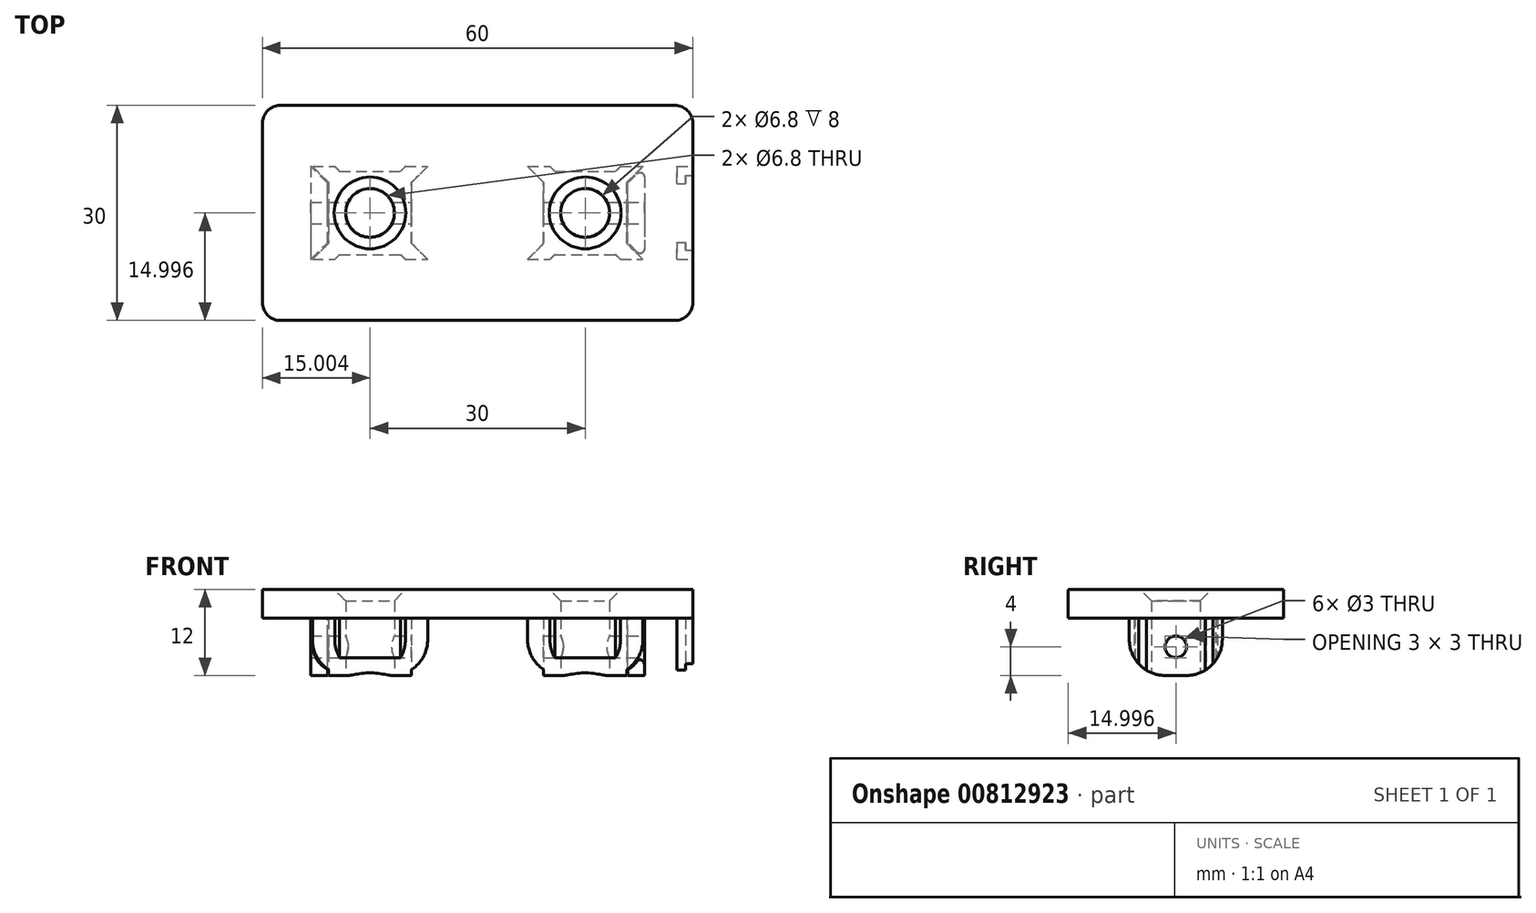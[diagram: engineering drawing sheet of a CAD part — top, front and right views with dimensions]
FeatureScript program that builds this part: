
annotation { "Feature Type Name" : "Feature", "Feature Type Description" : "" }
export const myFeature = defineFeature(function(context is Context, id is Id, definition is map)
    precondition{}
    {
        {
            var Q0;
            Q0=qCreatedBy(makeId("Top.planeOp"),FACE);
            var sketch = newSketch(context, id + "F0", { "sketchPlane" : qUnion([Q0])});
            skLineSegment(sketch, "E0", {"start": v(33.83, 0) * mm, "end": v(-26.14, 0) * mm, "construction": true});
            skLineSegment(sketch, "E1", {"start": v(0, -22.81) * mm, "end": v(0, 28.86) * mm, "construction": true});
            skLineSegment(sketch, "E2.bottom", {"start": v(0, -15) * mm, "end": v(-9.8, -15) * mm});
            skLineSegment(sketch, "E2.top", {"start": v(0, 15) * mm, "end": v(-9.8, 15) * mm});
            skLineSegment(sketch, "E2.right", {"start": v(-30, -12.5) * mm, "end": v(-30, -5.2) * mm});
            skPoint(sketch, "E2.middle", {"position": v(0, 0) * mm});
            skCircle(sketch, "E3", {"center": v(-15, 0) * mm, "radius": 3.4 * mm});
            skPoint(sketch, "E4.visualSharp", {"position": v(-30, 15) * mm});
            skArc(sketch, "E4.filletArc", {"start": v(-27.5, 15) * mm, "mid": v(-29.27, 14.27) * mm, "end": v(-30, 12.5) * mm});
            skPoint(sketch, "E5.visualSharp", {"position": v(-30, -15) * mm});
            skArc(sketch, "E5.filletArc", {"start": v(-30, -12.5) * mm, "mid": v(-29.27, -14.27) * mm, "end": v(-27.5, -15) * mm});
            skLineSegment(sketch, "E6.2", {"start": v(0, 12.8) * mm, "end": v(-4.55, 12.8) * mm});
            skLineSegment(sketch, "E6.5", {"start": v(-27.8, -8.25) * mm, "end": v(-27.8, -4.1) * mm});
            skLineSegment(sketch, "E6.7", {"start": v(0, -12.8) * mm, "end": v(-4.55, -12.8) * mm});
            skLineSegment(sketch, "E7", {"start": v(-4.55, 12.8) * mm, "end": v(-4.55, 8.9) * mm});
            skLineSegment(sketch, "E8", {"start": v(-4.55, 8.9) * mm, "end": v(-9.2, 4.24) * mm});
            skLineSegment(sketch, "E9", {"start": v(-9.2, 4.24) * mm, "end": v(-9.2, -4.24) * mm});
            skLineSegment(sketch, "E10", {"start": v(-9.2, -4.24) * mm, "end": v(-4.55, -8.9) * mm});
            skLineSegment(sketch, "E11", {"start": v(-4.55, -8.9) * mm, "end": v(-4.55, -12.8) * mm});
            skLineSegment(sketch, "E12", {"start": v(-15, -17.85) * mm, "end": v(-15, 20.15) * mm, "construction": true});
            skLineSegment(sketch, "E13", {"start": v(-20.2, 15) * mm, "end": v(-20.2, 14) * mm});
            skLineSegment(sketch, "E14", {"start": v(-20.2, 14) * mm, "end": v(-19.1, 14) * mm});
            skLineSegment(sketch, "E15", {"start": v(-19.1, 14) * mm, "end": v(-19.1, 12.8) * mm});
            skLineSegment(sketch, "E16.MirrorCS", {"start": v(-9.8, 15) * mm, "end": v(-9.8, 14) * mm});
            skLineSegment(sketch, "E17.MirrorCS", {"start": v(-9.8, 14) * mm, "end": v(-10.9, 14) * mm});
            skLineSegment(sketch, "E18.MirrorCS", {"start": v(-10.9, 14) * mm, "end": v(-10.9, 12.8) * mm});
            skLineSegment(sketch, "E19", {"start": v(-23.25, 12.8) * mm, "end": v(-23.25, 9.8) * mm});
            skLineSegment(sketch, "E20", {"start": v(-23.25, 9.8) * mm, "end": v(-19.24, 5.8) * mm});
            skLineSegment(sketch, "E21", {"start": v(-19.24, 5.8) * mm, "end": v(-10.76, 5.8) * mm});
            skLineSegment(sketch, "E22", {"start": v(-10.76, 5.8) * mm, "end": v(-6.75, 9.8) * mm});
            skLineSegment(sketch, "E23", {"start": v(-6.75, 9.8) * mm, "end": v(-6.75, 12.8) * mm});
            skLineSegment(sketch, "E24.1.0", {"start": v(-29, 5.2) * mm, "end": v(-29, 4.1) * mm});
            skLineSegment(sketch, "E24.1.1", {"start": v(-20.8, -4.24) * mm, "end": v(-20.8, 4.24) * mm});
            skLineSegment(sketch, "E24.1.2", {"start": v(-24.8, -8.25) * mm, "end": v(-20.8, -4.24) * mm});
            skLineSegment(sketch, "E24.1.3", {"start": v(-30, 5.2) * mm, "end": v(-29, 5.2) * mm});
            skLineSegment(sketch, "E24.1.4", {"start": v(-30, -5.2) * mm, "end": v(-29, -5.2) * mm});
            skLineSegment(sketch, "E24.1.5", {"start": v(-29, -5.2) * mm, "end": v(-29, -4.1) * mm});
            skLineSegment(sketch, "E24.1.6", {"start": v(-27.8, -8.25) * mm, "end": v(-24.8, -8.25) * mm});
            skLineSegment(sketch, "E24.1.7", {"start": v(-29, -4.1) * mm, "end": v(-27.8, -4.1) * mm});
            skLineSegment(sketch, "E24.1.8", {"start": v(-20.8, 4.24) * mm, "end": v(-24.8, 8.25) * mm});
            skLineSegment(sketch, "E24.1.9", {"start": v(-29, 4.1) * mm, "end": v(-27.8, 4.1) * mm});
            skLineSegment(sketch, "E24.1.10", {"start": v(-24.8, 8.25) * mm, "end": v(-27.8, 8.25) * mm});
            skLineSegment(sketch, "E24.2.0", {"start": v(-20.2, -14) * mm, "end": v(-19.1, -14) * mm});
            skLineSegment(sketch, "E24.2.1", {"start": v(-10.76, -5.8) * mm, "end": v(-19.24, -5.8) * mm});
            skLineSegment(sketch, "E24.2.2", {"start": v(-6.75, -9.8) * mm, "end": v(-10.76, -5.8) * mm});
            skLineSegment(sketch, "E24.2.3", {"start": v(-20.2, -15) * mm, "end": v(-20.2, -14) * mm});
            skLineSegment(sketch, "E24.2.4", {"start": v(-9.8, -15) * mm, "end": v(-9.8, -14) * mm});
            skLineSegment(sketch, "E24.2.5", {"start": v(-9.8, -14) * mm, "end": v(-10.9, -14) * mm});
            skLineSegment(sketch, "E24.2.6", {"start": v(-6.75, -12.8) * mm, "end": v(-6.75, -9.8) * mm});
            skLineSegment(sketch, "E24.2.7", {"start": v(-10.9, -14) * mm, "end": v(-10.9, -12.8) * mm});
            skLineSegment(sketch, "E24.2.8", {"start": v(-19.24, -5.8) * mm, "end": v(-23.25, -9.8) * mm});
            skLineSegment(sketch, "E24.2.9", {"start": v(-19.1, -14) * mm, "end": v(-19.1, -12.8) * mm});
            skLineSegment(sketch, "E24.2.10", {"start": v(-23.25, -9.8) * mm, "end": v(-23.25, -12.8) * mm});
            skLineSegment(sketch, "E25.trimOffspring", {"start": v(-27.8, 4.1) * mm, "end": v(-27.8, 8.25) * mm});
            skLineSegment(sketch, "E26.trimOffspring", {"start": v(-30, 5.2) * mm, "end": v(-30, 12.5) * mm});
            skLineSegment(sketch, "E27.trimOffspring", {"start": v(-19.1, -12.8) * mm, "end": v(-23.25, -12.8) * mm});
            skLineSegment(sketch, "E28.trimOffspring", {"start": v(-20.2, -15) * mm, "end": v(-27.5, -15) * mm});
            skLineSegment(sketch, "E29.trimOffspring", {"start": v(-20.2, 15) * mm, "end": v(-27.5, 15) * mm});
            skLineSegment(sketch, "E30.trimOffspring", {"start": v(-19.1, 12.8) * mm, "end": v(-23.25, 12.8) * mm});
            skLineSegment(sketch, "E31.trimOffspring", {"start": v(-6.75, 12.8) * mm, "end": v(-10.9, 12.8) * mm});
            skLineSegment(sketch, "E32.trimOffspring", {"start": v(-6.75, -12.8) * mm, "end": v(-10.9, -12.8) * mm});
            skLineSegment(sketch, "E33", {"start": v(-26.53, 17.8) * mm, "end": v(-26.53, 4.78) * mm, "construction": true});
            skLineSegment(sketch, "E34", {"start": v(-32.5, 11.53) * mm, "end": v(-19.6, 11.53) * mm, "construction": true});
            skLineSegment(sketch, "E35.bottom", {"start": v(-24.65, 9.65) * mm, "end": v(-28.4, 9.65) * mm});
            skLineSegment(sketch, "E35.top", {"start": v(-24.65, 13.4) * mm, "end": v(-28.4, 13.4) * mm});
            skLineSegment(sketch, "E35.left", {"start": v(-24.65, 9.65) * mm, "end": v(-24.65, 13.4) * mm});
            skLineSegment(sketch, "E35.right", {"start": v(-28.4, 9.65) * mm, "end": v(-28.4, 13.4) * mm});
            skPoint(sketch, "E35.middle", {"position": v(-26.53, 11.53) * mm});
            skLineSegment(sketch, "E36.MirrorCS", {"start": v(-28.4, -9.65) * mm, "end": v(-28.4, -13.4) * mm});
            skLineSegment(sketch, "E37.MirrorCS", {"start": v(-24.65, -13.4) * mm, "end": v(-28.4, -13.4) * mm});
            skLineSegment(sketch, "E38.MirrorCS", {"start": v(-24.65, -9.65) * mm, "end": v(-24.65, -13.4) * mm});
            skLineSegment(sketch, "E39.MirrorCS", {"start": v(-24.65, -9.65) * mm, "end": v(-28.4, -9.65) * mm});
            skLineSegment(sketch, "E40.MirrorCS", {"start": v(0, -15) * mm, "end": v(9.8, -15) * mm});
            skLineSegment(sketch, "E41.MirrorCS", {"start": v(0, -12.8) * mm, "end": v(4.55, -12.8) * mm});
            skLineSegment(sketch, "E42.MirrorCS", {"start": v(0, 12.8) * mm, "end": v(4.55, 12.8) * mm});
            skLineSegment(sketch, "E43.MirrorCS", {"start": v(0, 15) * mm, "end": v(9.8, 15) * mm});
            skLineSegment(sketch, "E44.MirrorCS", {"start": v(4.55, -8.9) * mm, "end": v(4.55, -12.8) * mm});
            skLineSegment(sketch, "E45.MirrorCS", {"start": v(4.55, 12.8) * mm, "end": v(4.55, 8.9) * mm});
            skLineSegment(sketch, "E46.MirrorCS", {"start": v(9.2, -4.24) * mm, "end": v(4.55, -8.9) * mm});
            skLineSegment(sketch, "E47.MirrorCS", {"start": v(9.2, 4.24) * mm, "end": v(9.2, -4.24) * mm});
            skLineSegment(sketch, "E48.MirrorCS", {"start": v(4.55, 8.9) * mm, "end": v(9.2, 4.24) * mm});
            skLineSegment(sketch, "E49.MirrorCS", {"start": v(6.75, -12.8) * mm, "end": v(6.75, -9.8) * mm});
            skLineSegment(sketch, "E50.MirrorCS", {"start": v(6.75, -9.8) * mm, "end": v(10.76, -5.8) * mm});
            skLineSegment(sketch, "E51.MirrorCS", {"start": v(10.76, -5.8) * mm, "end": v(19.24, -5.8) * mm});
            skLineSegment(sketch, "E52.MirrorCS", {"start": v(19.24, 5.8) * mm, "end": v(10.76, 5.8) * mm});
            skLineSegment(sketch, "E53.MirrorCS", {"start": v(10.76, 5.8) * mm, "end": v(6.75, 9.8) * mm});
            skLineSegment(sketch, "E54.MirrorCS", {"start": v(6.75, 9.8) * mm, "end": v(6.75, 12.8) * mm});
            skLineSegment(sketch, "E55.MirrorCS", {"start": v(6.75, 12.8) * mm, "end": v(10.9, 12.8) * mm});
            skLineSegment(sketch, "E56.MirrorCS", {"start": v(6.75, -12.8) * mm, "end": v(10.9, -12.8) * mm});
            skCircle(sketch, "E57.MirrorC", {"center": v(15, 0) * mm, "radius": 3.4 * mm});
            skLineSegment(sketch, "E58.MirrorCS", {"start": v(9.8, 15) * mm, "end": v(9.8, 14) * mm});
            skLineSegment(sketch, "E59.MirrorCS", {"start": v(9.8, 14) * mm, "end": v(10.9, 14) * mm});
            skLineSegment(sketch, "E60.MirrorCS", {"start": v(10.9, 14) * mm, "end": v(10.9, 12.8) * mm});
            skLineSegment(sketch, "E61.MirrorCS", {"start": v(10.9, -14) * mm, "end": v(10.9, -12.8) * mm});
            skLineSegment(sketch, "E62.MirrorCS", {"start": v(9.8, -14) * mm, "end": v(10.9, -14) * mm});
            skLineSegment(sketch, "E63.MirrorCS", {"start": v(9.8, -15) * mm, "end": v(9.8, -14) * mm});
            skLineSegment(sketch, "E64.MirrorCS", {"start": v(27.8, -8.25) * mm, "end": v(24.8, -8.25) * mm});
            skLineSegment(sketch, "E65.MirrorCS", {"start": v(24.8, -8.25) * mm, "end": v(20.8, -4.24) * mm});
            skLineSegment(sketch, "E66.MirrorCS", {"start": v(20.8, -4.24) * mm, "end": v(20.8, 4.24) * mm});
            skLineSegment(sketch, "E67.MirrorCS", {"start": v(20.8, 4.24) * mm, "end": v(24.8, 8.25) * mm});
            skLineSegment(sketch, "E68.MirrorCS", {"start": v(24.8, 8.25) * mm, "end": v(27.8, 8.25) * mm});
            skLineSegment(sketch, "E69.MirrorCS", {"start": v(27.8, 4.1) * mm, "end": v(27.8, 8.25) * mm});
            skLineSegment(sketch, "E70.MirrorCS", {"start": v(29, 4.1) * mm, "end": v(27.8, 4.1) * mm});
            skLineSegment(sketch, "E71.MirrorCS", {"start": v(29, 5.2) * mm, "end": v(29, 4.1) * mm});
            skLineSegment(sketch, "E72.MirrorCS", {"start": v(30, 5.2) * mm, "end": v(29, 5.2) * mm});
            skLineSegment(sketch, "E73.MirrorCS", {"start": v(30, 5.2) * mm, "end": v(30, 12.5) * mm});
            skLineSegment(sketch, "E74.MirrorCS", {"start": v(24.65, 9.65) * mm, "end": v(28.4, 9.65) * mm});
            skLineSegment(sketch, "E75.MirrorCS", {"start": v(28.4, 9.65) * mm, "end": v(28.4, 13.4) * mm});
            skLineSegment(sketch, "E76.MirrorCS", {"start": v(24.65, 13.4) * mm, "end": v(28.4, 13.4) * mm});
            skLineSegment(sketch, "E77.MirrorCS", {"start": v(24.65, 9.65) * mm, "end": v(24.65, 13.4) * mm});
            skArc(sketch, "E78.MirrorCS", {"start": v(27.5, 15) * mm, "mid": v(29.27, 14.27) * mm, "end": v(30, 12.5) * mm});
            skLineSegment(sketch, "E79.MirrorCS", {"start": v(23.25, 9.8) * mm, "end": v(19.24, 5.8) * mm});
            skLineSegment(sketch, "E80.MirrorCS", {"start": v(23.25, 12.8) * mm, "end": v(23.25, 9.8) * mm});
            skLineSegment(sketch, "E81.MirrorCS", {"start": v(19.1, 12.8) * mm, "end": v(23.25, 12.8) * mm});
            skLineSegment(sketch, "E82.MirrorCS", {"start": v(20.2, 15) * mm, "end": v(27.5, 15) * mm});
            skLineSegment(sketch, "E83.MirrorCS", {"start": v(20.2, 15) * mm, "end": v(20.2, 14) * mm});
            skLineSegment(sketch, "E84.MirrorCS", {"start": v(23.25, -9.8) * mm, "end": v(23.25, -12.8) * mm});
            skLineSegment(sketch, "E85.MirrorCS", {"start": v(20.2, 14) * mm, "end": v(19.1, 14) * mm});
            skLineSegment(sketch, "E86.MirrorCS", {"start": v(19.1, 14) * mm, "end": v(19.1, 12.8) * mm});
            skLineSegment(sketch, "E87.MirrorCS", {"start": v(19.24, -5.8) * mm, "end": v(23.25, -9.8) * mm});
            skLineSegment(sketch, "E88.MirrorCS", {"start": v(19.1, -12.8) * mm, "end": v(23.25, -12.8) * mm});
            skLineSegment(sketch, "E89.MirrorCS", {"start": v(19.1, -14) * mm, "end": v(19.1, -12.8) * mm});
            skLineSegment(sketch, "E90.MirrorCS", {"start": v(20.2, -14) * mm, "end": v(19.1, -14) * mm});
            skLineSegment(sketch, "E91.MirrorCS", {"start": v(20.2, -15) * mm, "end": v(20.2, -14) * mm});
            skLineSegment(sketch, "E92.MirrorCS", {"start": v(20.2, -15) * mm, "end": v(27.5, -15) * mm});
            skLineSegment(sketch, "E93.MirrorCS", {"start": v(27.8, -8.25) * mm, "end": v(27.8, -4.1) * mm});
            skLineSegment(sketch, "E94.MirrorCS", {"start": v(29, -4.1) * mm, "end": v(27.8, -4.1) * mm});
            skLineSegment(sketch, "E95.MirrorCS", {"start": v(30, -5.2) * mm, "end": v(29, -5.2) * mm});
            skLineSegment(sketch, "E96.MirrorCS", {"start": v(30, -12.5) * mm, "end": v(30, -5.2) * mm});
            skArc(sketch, "E97.MirrorCS", {"start": v(30, -12.5) * mm, "mid": v(29.27, -14.27) * mm, "end": v(27.5, -15) * mm});
            skLineSegment(sketch, "E98.MirrorCS", {"start": v(29, -5.2) * mm, "end": v(29, -4.1) * mm});
            skLineSegment(sketch, "E99.MirrorCS", {"start": v(24.65, -9.65) * mm, "end": v(28.4, -9.65) * mm});
            skLineSegment(sketch, "E100.MirrorCS", {"start": v(28.4, -9.65) * mm, "end": v(28.4, -13.4) * mm});
            skLineSegment(sketch, "E101.MirrorCS", {"start": v(24.65, -13.4) * mm, "end": v(28.4, -13.4) * mm});
            skLineSegment(sketch, "E102.MirrorCS", {"start": v(24.65, -9.65) * mm, "end": v(24.65, -13.4) * mm});
            skSolve(sketch);
        }
        {
            var Q0;
            Q0 = qSketchRegion(id + "F0", true);
            extrude(context, id + "F1", {"entities" : qUnion([Q0]), "depth" : 400 * mm, "offsetDistance" : 25 * mm});
        }
        {
            var Q0;
            Q0=qCreatedBy(makeId("Top.planeOp"),FACE);
            var sketch = newSketch(context, id + "F2", { "sketchPlane" : qUnion([Q0])});
            skLineSegment(sketch, "E103", {"start": v(34.68, -0.36) * mm, "end": v(-25.29, -0.36) * mm, "construction": true});
            skLineSegment(sketch, "E104", {"start": v(0.85, -23.18) * mm, "end": v(0.85, 28.5) * mm, "construction": true});
            skLineSegment(sketch, "E105.bottom", {"start": v(0.85, -15.36) * mm, "end": v(-8.95, -15.36) * mm});
            skLineSegment(sketch, "E105.top", {"start": v(0.85, 14.64) * mm, "end": v(-8.95, 14.64) * mm});
            skLineSegment(sketch, "E105.right", {"start": v(-29.15, -12.86) * mm, "end": v(-29.15, -5.56) * mm});
            skPoint(sketch, "E105.middle", {"position": v(0.85, -0.36) * mm});
            skCircle(sketch, "E106", {"center": v(-14.15, -0.36) * mm, "radius": 3.4 * mm});
            skPoint(sketch, "E107.visualSharp", {"position": v(-29.15, 14.64) * mm});
            skArc(sketch, "E107.filletArc", {"start": v(-26.65, 14.64) * mm, "mid": v(-28.41, 13.9) * mm, "end": v(-29.15, 12.14) * mm});
            skPoint(sketch, "E108.visualSharp", {"position": v(-29.15, -15.36) * mm});
            skArc(sketch, "E108.filletArc", {"start": v(-29.15, -12.86) * mm, "mid": v(-28.41, -14.63) * mm, "end": v(-26.65, -15.36) * mm});
            skLineSegment(sketch, "E109.2", {"start": v(0.85, 12.44) * mm, "end": v(-3.7, 12.44) * mm});
            skLineSegment(sketch, "E109.5", {"start": v(-26.95, -8.61) * mm, "end": v(-26.95, -4.46) * mm});
            skLineSegment(sketch, "E109.7", {"start": v(0.85, -13.16) * mm, "end": v(-3.7, -13.16) * mm});
            skLineSegment(sketch, "E110", {"start": v(-3.7, 12.44) * mm, "end": v(-3.7, 8.53) * mm});
            skLineSegment(sketch, "E111", {"start": v(-3.7, 8.53) * mm, "end": v(-8.35, 3.88) * mm});
            skLineSegment(sketch, "E112", {"start": v(-8.35, 3.88) * mm, "end": v(-8.35, -4.6) * mm});
            skLineSegment(sketch, "E113", {"start": v(-8.35, -4.6) * mm, "end": v(-3.7, -9.26) * mm});
            skLineSegment(sketch, "E114", {"start": v(-3.7, -9.26) * mm, "end": v(-3.7, -13.16) * mm});
            skLineSegment(sketch, "E115", {"start": v(-14.15, -18.21) * mm, "end": v(-14.15, 19.79) * mm, "construction": true});
            skLineSegment(sketch, "E116", {"start": v(-19.35, 14.64) * mm, "end": v(-19.35, 13.64) * mm});
            skLineSegment(sketch, "E117", {"start": v(-19.35, 13.64) * mm, "end": v(-18.25, 13.64) * mm});
            skLineSegment(sketch, "E118", {"start": v(-18.25, 13.64) * mm, "end": v(-18.25, 12.44) * mm});
            skLineSegment(sketch, "E119.MirrorCS", {"start": v(-8.95, 14.64) * mm, "end": v(-8.95, 13.64) * mm});
            skLineSegment(sketch, "E120.MirrorCS", {"start": v(-8.95, 13.64) * mm, "end": v(-10.05, 13.64) * mm});
            skLineSegment(sketch, "E121.MirrorCS", {"start": v(-10.05, 13.64) * mm, "end": v(-10.05, 12.44) * mm});
            skLineSegment(sketch, "E122", {"start": v(-22.4, 12.44) * mm, "end": v(-22.4, 9.44) * mm});
            skLineSegment(sketch, "E123", {"start": v(-22.4, 9.44) * mm, "end": v(-18.4, 5.44) * mm});
            skLineSegment(sketch, "E124", {"start": v(-18.4, 5.44) * mm, "end": v(-9.9, 5.44) * mm});
            skLineSegment(sketch, "E125", {"start": v(-9.9, 5.44) * mm, "end": v(-5.9, 9.44) * mm});
            skLineSegment(sketch, "E126", {"start": v(-5.9, 9.44) * mm, "end": v(-5.9, 12.44) * mm});
            skLineSegment(sketch, "E127.1.0", {"start": v(-28.15, 4.84) * mm, "end": v(-28.15, 3.74) * mm});
            skLineSegment(sketch, "E127.1.1", {"start": v(-19.95, -4.6) * mm, "end": v(-19.95, 3.88) * mm});
            skLineSegment(sketch, "E127.1.2", {"start": v(-23.95, -8.61) * mm, "end": v(-19.95, -4.6) * mm});
            skLineSegment(sketch, "E127.1.3", {"start": v(-29.15, 4.84) * mm, "end": v(-28.15, 4.84) * mm});
            skLineSegment(sketch, "E127.1.4", {"start": v(-29.15, -5.56) * mm, "end": v(-28.15, -5.56) * mm});
            skLineSegment(sketch, "E127.1.5", {"start": v(-28.15, -5.56) * mm, "end": v(-28.15, -4.46) * mm});
            skLineSegment(sketch, "E127.1.6", {"start": v(-26.95, -8.61) * mm, "end": v(-23.95, -8.61) * mm});
            skLineSegment(sketch, "E127.1.7", {"start": v(-28.15, -4.46) * mm, "end": v(-26.95, -4.46) * mm});
            skLineSegment(sketch, "E127.1.8", {"start": v(-19.95, 3.88) * mm, "end": v(-23.95, 7.89) * mm});
            skLineSegment(sketch, "E127.1.9", {"start": v(-28.15, 3.74) * mm, "end": v(-26.95, 3.74) * mm});
            skLineSegment(sketch, "E127.1.10", {"start": v(-23.95, 7.89) * mm, "end": v(-26.95, 7.89) * mm});
            skLineSegment(sketch, "E127.2.0", {"start": v(-19.35, -14.36) * mm, "end": v(-18.25, -14.36) * mm});
            skLineSegment(sketch, "E127.2.1", {"start": v(-9.9, -6.16) * mm, "end": v(-18.4, -6.16) * mm});
            skLineSegment(sketch, "E127.2.2", {"start": v(-5.9, -10.17) * mm, "end": v(-9.9, -6.16) * mm});
            skLineSegment(sketch, "E127.2.3", {"start": v(-19.35, -15.36) * mm, "end": v(-19.35, -14.36) * mm});
            skLineSegment(sketch, "E127.2.4", {"start": v(-8.95, -15.36) * mm, "end": v(-8.95, -14.36) * mm});
            skLineSegment(sketch, "E127.2.5", {"start": v(-8.95, -14.36) * mm, "end": v(-10.05, -14.36) * mm});
            skLineSegment(sketch, "E127.2.6", {"start": v(-5.9, -13.16) * mm, "end": v(-5.9, -10.17) * mm});
            skLineSegment(sketch, "E127.2.7", {"start": v(-10.05, -14.36) * mm, "end": v(-10.05, -13.16) * mm});
            skLineSegment(sketch, "E127.2.8", {"start": v(-18.4, -6.16) * mm, "end": v(-22.4, -10.17) * mm});
            skLineSegment(sketch, "E127.2.9", {"start": v(-18.25, -14.36) * mm, "end": v(-18.25, -13.16) * mm});
            skLineSegment(sketch, "E127.2.10", {"start": v(-22.4, -10.17) * mm, "end": v(-22.4, -13.16) * mm});
            skLineSegment(sketch, "E128.trimOffspring", {"start": v(-26.95, 3.74) * mm, "end": v(-26.95, 7.89) * mm});
            skLineSegment(sketch, "E129.trimOffspring", {"start": v(-29.15, 4.84) * mm, "end": v(-29.15, 12.14) * mm});
            skLineSegment(sketch, "E130.trimOffspring", {"start": v(-18.25, -13.16) * mm, "end": v(-22.4, -13.16) * mm});
            skLineSegment(sketch, "E131.trimOffspring", {"start": v(-19.35, -15.36) * mm, "end": v(-26.65, -15.36) * mm});
            skLineSegment(sketch, "E132.trimOffspring", {"start": v(-19.35, 14.64) * mm, "end": v(-26.65, 14.64) * mm});
            skLineSegment(sketch, "E133.trimOffspring", {"start": v(-18.25, 12.44) * mm, "end": v(-22.4, 12.44) * mm});
            skLineSegment(sketch, "E134.trimOffspring", {"start": v(-5.9, 12.44) * mm, "end": v(-10.05, 12.44) * mm});
            skLineSegment(sketch, "E135.trimOffspring", {"start": v(-5.9, -13.16) * mm, "end": v(-10.05, -13.16) * mm});
            skLineSegment(sketch, "E136", {"start": v(-25.67, 17.43) * mm, "end": v(-25.67, 4.42) * mm, "construction": true});
            skLineSegment(sketch, "E137", {"start": v(-31.64, 11.16) * mm, "end": v(-18.74, 11.16) * mm, "construction": true});
            skLineSegment(sketch, "E138.bottom", {"start": v(-23.8, 9.29) * mm, "end": v(-27.55, 9.29) * mm});
            skLineSegment(sketch, "E138.top", {"start": v(-23.8, 13.04) * mm, "end": v(-27.55, 13.04) * mm});
            skLineSegment(sketch, "E138.left", {"start": v(-23.8, 9.29) * mm, "end": v(-23.8, 13.04) * mm});
            skLineSegment(sketch, "E138.right", {"start": v(-27.55, 9.29) * mm, "end": v(-27.55, 13.04) * mm});
            skPoint(sketch, "E138.middle", {"position": v(-25.67, 11.16) * mm});
            skLineSegment(sketch, "E139.MirrorCS", {"start": v(-27.55, -10.01) * mm, "end": v(-27.55, -13.76) * mm});
            skLineSegment(sketch, "E140.MirrorCS", {"start": v(-23.8, -13.76) * mm, "end": v(-27.55, -13.76) * mm});
            skLineSegment(sketch, "E141.MirrorCS", {"start": v(-23.8, -10.01) * mm, "end": v(-23.8, -13.76) * mm});
            skLineSegment(sketch, "E142.MirrorCS", {"start": v(-23.8, -10.01) * mm, "end": v(-27.55, -10.01) * mm});
            skLineSegment(sketch, "E143.MirrorCS", {"start": v(0.85, -15.36) * mm, "end": v(10.65, -15.36) * mm});
            skLineSegment(sketch, "E144.MirrorCS", {"start": v(0.85, -13.16) * mm, "end": v(5.4, -13.16) * mm});
            skLineSegment(sketch, "E145.MirrorCS", {"start": v(0.85, 12.44) * mm, "end": v(5.4, 12.44) * mm});
            skLineSegment(sketch, "E146.MirrorCS", {"start": v(0.85, 14.64) * mm, "end": v(10.65, 14.64) * mm});
            skLineSegment(sketch, "E147.MirrorCS", {"start": v(5.4, -9.26) * mm, "end": v(5.4, -13.16) * mm});
            skLineSegment(sketch, "E148.MirrorCS", {"start": v(5.4, 12.44) * mm, "end": v(5.4, 8.53) * mm});
            skLineSegment(sketch, "E149.MirrorCS", {"start": v(10.05, -4.6) * mm, "end": v(5.4, -9.26) * mm});
            skLineSegment(sketch, "E150.MirrorCS", {"start": v(10.05, 3.88) * mm, "end": v(10.05, -4.6) * mm});
            skLineSegment(sketch, "E151.MirrorCS", {"start": v(5.4, 8.53) * mm, "end": v(10.05, 3.88) * mm});
            skLineSegment(sketch, "E152.MirrorCS", {"start": v(7.6, -13.16) * mm, "end": v(7.6, -10.17) * mm});
            skLineSegment(sketch, "E153.MirrorCS", {"start": v(7.6, -10.17) * mm, "end": v(11.6, -6.16) * mm});
            skLineSegment(sketch, "E154.MirrorCS", {"start": v(11.6, -6.16) * mm, "end": v(20.1, -6.16) * mm});
            skLineSegment(sketch, "E155.MirrorCS", {"start": v(20.1, 5.44) * mm, "end": v(11.6, 5.44) * mm});
            skLineSegment(sketch, "E156.MirrorCS", {"start": v(11.6, 5.44) * mm, "end": v(7.6, 9.44) * mm});
            skLineSegment(sketch, "E157.MirrorCS", {"start": v(7.6, 9.44) * mm, "end": v(7.6, 12.44) * mm});
            skLineSegment(sketch, "E158.MirrorCS", {"start": v(7.6, 12.44) * mm, "end": v(11.75, 12.44) * mm});
            skLineSegment(sketch, "E159.MirrorCS", {"start": v(7.6, -13.16) * mm, "end": v(11.75, -13.16) * mm});
            skCircle(sketch, "E160.MirrorC", {"center": v(15.85, -0.36) * mm, "radius": 3.4 * mm});
            skLineSegment(sketch, "E161.MirrorCS", {"start": v(10.65, 14.64) * mm, "end": v(10.65, 13.64) * mm});
            skLineSegment(sketch, "E162.MirrorCS", {"start": v(10.65, 13.64) * mm, "end": v(11.75, 13.64) * mm});
            skLineSegment(sketch, "E163.MirrorCS", {"start": v(11.75, 13.64) * mm, "end": v(11.75, 12.44) * mm});
            skLineSegment(sketch, "E164.MirrorCS", {"start": v(11.75, -14.36) * mm, "end": v(11.75, -13.16) * mm});
            skLineSegment(sketch, "E165.MirrorCS", {"start": v(10.65, -14.36) * mm, "end": v(11.75, -14.36) * mm});
            skLineSegment(sketch, "E166.MirrorCS", {"start": v(10.65, -15.36) * mm, "end": v(10.65, -14.36) * mm});
            skLineSegment(sketch, "E167.MirrorCS", {"start": v(28.65, -8.61) * mm, "end": v(25.66, -8.61) * mm});
            skLineSegment(sketch, "E168.MirrorCS", {"start": v(25.66, -8.61) * mm, "end": v(21.65, -4.6) * mm});
            skLineSegment(sketch, "E169.MirrorCS", {"start": v(21.65, -4.6) * mm, "end": v(21.65, 3.88) * mm});
            skLineSegment(sketch, "E170.MirrorCS", {"start": v(21.65, 3.88) * mm, "end": v(25.66, 7.89) * mm});
            skLineSegment(sketch, "E171.MirrorCS", {"start": v(25.66, 7.89) * mm, "end": v(28.65, 7.89) * mm});
            skLineSegment(sketch, "E172.MirrorCS", {"start": v(28.65, 3.74) * mm, "end": v(28.65, 7.89) * mm});
            skLineSegment(sketch, "E173.MirrorCS", {"start": v(29.85, 3.74) * mm, "end": v(28.65, 3.74) * mm});
            skLineSegment(sketch, "E174.MirrorCS", {"start": v(29.85, 4.84) * mm, "end": v(29.85, 3.74) * mm});
            skLineSegment(sketch, "E175.MirrorCS", {"start": v(30.85, 4.84) * mm, "end": v(29.85, 4.84) * mm});
            skLineSegment(sketch, "E176.MirrorCS", {"start": v(30.85, 4.84) * mm, "end": v(30.85, 12.14) * mm});
            skLineSegment(sketch, "E177.MirrorCS", {"start": v(25.5, 9.29) * mm, "end": v(29.25, 9.29) * mm});
            skLineSegment(sketch, "E178.MirrorCS", {"start": v(29.25, 9.29) * mm, "end": v(29.25, 13.04) * mm});
            skLineSegment(sketch, "E179.MirrorCS", {"start": v(25.5, 13.04) * mm, "end": v(29.25, 13.04) * mm});
            skLineSegment(sketch, "E180.MirrorCS", {"start": v(25.5, 9.29) * mm, "end": v(25.5, 13.04) * mm});
            skArc(sketch, "E181.MirrorCS", {"start": v(28.35, 14.64) * mm, "mid": v(30.12, 13.9) * mm, "end": v(30.85, 12.14) * mm});
            skLineSegment(sketch, "E182.MirrorCS", {"start": v(24.1, 9.44) * mm, "end": v(20.1, 5.44) * mm});
            skLineSegment(sketch, "E183.MirrorCS", {"start": v(24.1, 12.44) * mm, "end": v(24.1, 9.44) * mm});
            skLineSegment(sketch, "E184.MirrorCS", {"start": v(19.95, 12.44) * mm, "end": v(24.1, 12.44) * mm});
            skLineSegment(sketch, "E185.MirrorCS", {"start": v(21.05, 14.64) * mm, "end": v(28.35, 14.64) * mm});
            skLineSegment(sketch, "E186.MirrorCS", {"start": v(21.05, 14.64) * mm, "end": v(21.05, 13.64) * mm});
            skLineSegment(sketch, "E187.MirrorCS", {"start": v(24.1, -10.17) * mm, "end": v(24.1, -13.16) * mm});
            skLineSegment(sketch, "E188.MirrorCS", {"start": v(21.05, 13.64) * mm, "end": v(19.95, 13.64) * mm});
            skLineSegment(sketch, "E189.MirrorCS", {"start": v(19.95, 13.64) * mm, "end": v(19.95, 12.44) * mm});
            skLineSegment(sketch, "E190.MirrorCS", {"start": v(20.1, -6.16) * mm, "end": v(24.1, -10.17) * mm});
            skLineSegment(sketch, "E191.MirrorCS", {"start": v(19.95, -13.16) * mm, "end": v(24.1, -13.16) * mm});
            skLineSegment(sketch, "E192.MirrorCS", {"start": v(19.95, -14.36) * mm, "end": v(19.95, -13.16) * mm});
            skLineSegment(sketch, "E193.MirrorCS", {"start": v(21.05, -14.36) * mm, "end": v(19.95, -14.36) * mm});
            skLineSegment(sketch, "E194.MirrorCS", {"start": v(21.05, -15.36) * mm, "end": v(21.05, -14.36) * mm});
            skLineSegment(sketch, "E195.MirrorCS", {"start": v(21.05, -15.36) * mm, "end": v(28.35, -15.36) * mm});
            skLineSegment(sketch, "E196.MirrorCS", {"start": v(28.65, -8.61) * mm, "end": v(28.65, -4.46) * mm});
            skLineSegment(sketch, "E197.MirrorCS", {"start": v(29.85, -4.46) * mm, "end": v(28.65, -4.46) * mm});
            skLineSegment(sketch, "E198.MirrorCS", {"start": v(30.85, -5.56) * mm, "end": v(29.85, -5.56) * mm});
            skLineSegment(sketch, "E199.MirrorCS", {"start": v(30.85, -12.86) * mm, "end": v(30.85, -5.56) * mm});
            skArc(sketch, "E200.MirrorCS", {"start": v(30.85, -12.86) * mm, "mid": v(30.12, -14.63) * mm, "end": v(28.35, -15.36) * mm});
            skLineSegment(sketch, "E201.MirrorCS", {"start": v(29.85, -5.56) * mm, "end": v(29.85, -4.46) * mm});
            skLineSegment(sketch, "E202.MirrorCS", {"start": v(25.5, -10.01) * mm, "end": v(29.25, -10.01) * mm});
            skLineSegment(sketch, "E203.MirrorCS", {"start": v(29.25, -10.01) * mm, "end": v(29.25, -13.76) * mm});
            skLineSegment(sketch, "E204.MirrorCS", {"start": v(25.5, -13.76) * mm, "end": v(29.25, -13.76) * mm});
            skLineSegment(sketch, "E205.MirrorCS", {"start": v(25.5, -10.01) * mm, "end": v(25.5, -13.76) * mm});
            skSolve(sketch);
        }
        {
            var Q0;
            Q0 = qSketchRegion(id + "F2", true);
            extrude(context, id + "F3", {"entities" : qUnion([Q0]), "depth" : 300 * mm, "offsetDistance" : 25 * mm});
        }
        {
            var Q0;
            Q0=makeQuery(id+"F3.opExtrude","SWEPT_BODY",BODY,{"disambiguationData":[OSD([sQuery(id+"F2.wireOp",EDGE,"E105.bottom"),sQuery(id+"F2.wireOp",EDGE,"E105.top"),sQuery(id+"F2.wireOp",EDGE,"E105.right"),sQuery(id+"F2.wireOp",EDGE,"E106"),sQuery(id+"F2.wireOp",EDGE,"E107.filletArc"),sQuery(id+"F2.wireOp",EDGE,"E108.filletArc"),sQuery(id+"F2.wireOp",EDGE,"E109.2"),sQuery(id+"F2.wireOp",EDGE,"E109.5"),sQuery(id+"F2.wireOp",EDGE,"E109.7"),sQuery(id+"F2.wireOp",EDGE,"E110"),sQuery(id+"F2.wireOp",EDGE,"E112"),sQuery(id+"F2.wireOp",EDGE,"E113"),sQuery(id+"F2.wireOp",EDGE,"E114"),sQuery(id+"F2.wireOp",EDGE,"E117"),sQuery(id+"F2.wireOp",EDGE,"E118"),sQuery(id+"F2.wireOp",EDGE,"E119.MirrorCS"),sQuery(id+"F2.wireOp",EDGE,"E120.MirrorCS"),sQuery(id+"F2.wireOp",EDGE,"E121.MirrorCS"),sQuery(id+"F2.wireOp",EDGE,"E122"),sQuery(id+"F2.wireOp",EDGE,"E123"),sQuery(id+"F2.wireOp",EDGE,"E124"),sQuery(id+"F2.wireOp",EDGE,"E125"),sQuery(id+"F2.wireOp",EDGE,"E126"),sQuery(id+"F2.wireOp",EDGE,"E127.1.0"),sQuery(id+"F2.wireOp",EDGE,"E127.1.1"),sQuery(id+"F2.wireOp",EDGE,"E127.1.2"),sQuery(id+"F2.wireOp",EDGE,"E127.1.3"),sQuery(id+"F2.wireOp",EDGE,"E127.1.4"),sQuery(id+"F2.wireOp",EDGE,"E127.1.5"),sQuery(id+"F2.wireOp",EDGE,"E127.1.6"),sQuery(id+"F2.wireOp",EDGE,"E127.1.7"),sQuery(id+"F2.wireOp",EDGE,"E127.1.8"),sQuery(id+"F2.wireOp",EDGE,"E127.1.9"),sQuery(id+"F2.wireOp",EDGE,"E127.1.10"),sQuery(id+"F2.wireOp",EDGE,"E127.2.0"),sQuery(id+"F2.wireOp",EDGE,"E127.2.1"),sQuery(id+"F2.wireOp",EDGE,"E127.2.2"),sQuery(id+"F2.wireOp",EDGE,"E127.2.3"),sQuery(id+"F2.wireOp",EDGE,"E127.2.4"),sQuery(id+"F2.wireOp",EDGE,"E127.2.5"),sQuery(id+"F2.wireOp",EDGE,"E127.2.6"),sQuery(id+"F2.wireOp",EDGE,"E127.2.7"),sQuery(id+"F2.wireOp",EDGE,"E127.2.8"),sQuery(id+"F2.wireOp",EDGE,"E127.2.9"),sQuery(id+"F2.wireOp",EDGE,"E127.2.10"),sQuery(id+"F2.wireOp",EDGE,"E128.trimOffspring"),sQuery(id+"F2.wireOp",EDGE,"E129.trimOffspring"),sQuery(id+"F2.wireOp",EDGE,"E130.trimOffspring"),sQuery(id+"F2.wireOp",EDGE,"E131.trimOffspring"),sQuery(id+"F2.wireOp",EDGE,"E132.trimOffspring"),sQuery(id+"F2.wireOp",EDGE,"E133.trimOffspring"),sQuery(id+"F2.wireOp",EDGE,"E134.trimOffspring"),sQuery(id+"F2.wireOp",EDGE,"E135.trimOffspring"),sQuery(id+"F2.wireOp",EDGE,"E138.bottom"),sQuery(id+"F2.wireOp",EDGE,"E138.top"),sQuery(id+"F2.wireOp",EDGE,"E138.left"),sQuery(id+"F2.wireOp",EDGE,"E138.right"),sQuery(id+"F2.wireOp",EDGE,"E139.MirrorCS"),sQuery(id+"F2.wireOp",EDGE,"E116"),sQuery(id+"F2.wireOp",EDGE,"E140.MirrorCS"),sQuery(id+"F2.wireOp",EDGE,"E141.MirrorCS"),sQuery(id+"F2.wireOp",EDGE,"E142.MirrorCS"),sQuery(id+"F2.wireOp",EDGE,"E143.MirrorCS"),sQuery(id+"F2.wireOp",EDGE,"E144.MirrorCS"),sQuery(id+"F2.wireOp",EDGE,"E145.MirrorCS"),sQuery(id+"F2.wireOp",EDGE,"E146.MirrorCS"),sQuery(id+"F2.wireOp",EDGE,"E147.MirrorCS"),sQuery(id+"F2.wireOp",EDGE,"E148.MirrorCS"),sQuery(id+"F2.wireOp",EDGE,"E149.MirrorCS"),sQuery(id+"F2.wireOp",EDGE,"E150.MirrorCS"),sQuery(id+"F2.wireOp",EDGE,"E151.MirrorCS"),sQuery(id+"F2.wireOp",EDGE,"E152.MirrorCS"),sQuery(id+"F2.wireOp",EDGE,"E153.MirrorCS"),sQuery(id+"F2.wireOp",EDGE,"E154.MirrorCS"),sQuery(id+"F2.wireOp",EDGE,"E155.MirrorCS"),sQuery(id+"F2.wireOp",EDGE,"E156.MirrorCS"),sQuery(id+"F2.wireOp",EDGE,"E157.MirrorCS"),sQuery(id+"F2.wireOp",EDGE,"E158.MirrorCS"),sQuery(id+"F2.wireOp",EDGE,"E159.MirrorCS"),sQuery(id+"F2.wireOp",EDGE,"E160.MirrorC"),sQuery(id+"F2.wireOp",EDGE,"E161.MirrorCS"),sQuery(id+"F2.wireOp",EDGE,"E162.MirrorCS"),sQuery(id+"F2.wireOp",EDGE,"E163.MirrorCS"),sQuery(id+"F2.wireOp",EDGE,"E164.MirrorCS"),sQuery(id+"F2.wireOp",EDGE,"E165.MirrorCS"),sQuery(id+"F2.wireOp",EDGE,"E166.MirrorCS"),sQuery(id+"F2.wireOp",EDGE,"E168.MirrorCS"),sQuery(id+"F2.wireOp",EDGE,"E169.MirrorCS"),sQuery(id+"F2.wireOp",EDGE,"E170.MirrorCS"),sQuery(id+"F2.wireOp",EDGE,"E171.MirrorCS"),sQuery(id+"F2.wireOp",EDGE,"E172.MirrorCS"),sQuery(id+"F2.wireOp",EDGE,"E173.MirrorCS"),sQuery(id+"F2.wireOp",EDGE,"E174.MirrorCS"),sQuery(id+"F2.wireOp",EDGE,"E175.MirrorCS"),sQuery(id+"F2.wireOp",EDGE,"E176.MirrorCS"),sQuery(id+"F2.wireOp",EDGE,"E177.MirrorCS"),sQuery(id+"F2.wireOp",EDGE,"E178.MirrorCS"),sQuery(id+"F2.wireOp",EDGE,"E179.MirrorCS"),sQuery(id+"F2.wireOp",EDGE,"E180.MirrorCS"),sQuery(id+"F2.wireOp",EDGE,"E181.MirrorCS"),sQuery(id+"F2.wireOp",EDGE,"E182.MirrorCS"),sQuery(id+"F2.wireOp",EDGE,"E183.MirrorCS"),sQuery(id+"F2.wireOp",EDGE,"E184.MirrorCS"),sQuery(id+"F2.wireOp",EDGE,"E185.MirrorCS"),sQuery(id+"F2.wireOp",EDGE,"E186.MirrorCS"),sQuery(id+"F2.wireOp",EDGE,"E187.MirrorCS"),sQuery(id+"F2.wireOp",EDGE,"E188.MirrorCS"),sQuery(id+"F2.wireOp",EDGE,"E189.MirrorCS"),sQuery(id+"F2.wireOp",EDGE,"E190.MirrorCS"),sQuery(id+"F2.wireOp",EDGE,"E191.MirrorCS"),sQuery(id+"F2.wireOp",EDGE,"E192.MirrorCS"),sQuery(id+"F2.wireOp",EDGE,"E193.MirrorCS"),sQuery(id+"F2.wireOp",EDGE,"E111"),sQuery(id+"F2.wireOp",EDGE,"E194.MirrorCS"),sQuery(id+"F2.wireOp",EDGE,"E195.MirrorCS"),sQuery(id+"F2.wireOp",EDGE,"E167.MirrorCS"),sQuery(id+"F2.wireOp",EDGE,"E196.MirrorCS"),sQuery(id+"F2.wireOp",EDGE,"E197.MirrorCS"),sQuery(id+"F2.wireOp",EDGE,"E198.MirrorCS"),sQuery(id+"F2.wireOp",EDGE,"E199.MirrorCS"),sQuery(id+"F2.wireOp",EDGE,"E200.MirrorCS"),sQuery(id+"F2.wireOp",EDGE,"E201.MirrorCS"),sQuery(id+"F2.wireOp",EDGE,"E202.MirrorCS"),sQuery(id+"F2.wireOp",EDGE,"E203.MirrorCS"),sQuery(id+"F2.wireOp",EDGE,"E204.MirrorCS"),sQuery(id+"F2.wireOp",EDGE,"E205.MirrorCS")])]});
            var Q1;
            Q1=qCreatedBy(makeId("Front.planeOp"),FACE);
            transform(context, id + "F4", {"entities" : qUnion([Q0]), "transformType" : TransformType.TRANSLATION_DISTANCE, "transformDirection" : qUnion([Q1]), "distance" : 60 * mm, "makeCopy" : false});
        }
        {
            var Q0;
            Q0=makeQuery(id+"F3.opExtrude","CAP_FACE",FACE,{"disambiguationData":[OSD([sQuery(id+"F2.wireOp",EDGE,"E105.bottom"),sQuery(id+"F2.wireOp",EDGE,"E105.top"),sQuery(id+"F2.wireOp",EDGE,"E105.right"),sQuery(id+"F2.wireOp",EDGE,"E106"),sQuery(id+"F2.wireOp",EDGE,"E107.filletArc"),sQuery(id+"F2.wireOp",EDGE,"E108.filletArc"),sQuery(id+"F2.wireOp",EDGE,"E109.2"),sQuery(id+"F2.wireOp",EDGE,"E109.5"),sQuery(id+"F2.wireOp",EDGE,"E109.7"),sQuery(id+"F2.wireOp",EDGE,"E110"),sQuery(id+"F2.wireOp",EDGE,"E112"),sQuery(id+"F2.wireOp",EDGE,"E113"),sQuery(id+"F2.wireOp",EDGE,"E114"),sQuery(id+"F2.wireOp",EDGE,"E117"),sQuery(id+"F2.wireOp",EDGE,"E118"),sQuery(id+"F2.wireOp",EDGE,"E119.MirrorCS"),sQuery(id+"F2.wireOp",EDGE,"E120.MirrorCS"),sQuery(id+"F2.wireOp",EDGE,"E121.MirrorCS"),sQuery(id+"F2.wireOp",EDGE,"E122"),sQuery(id+"F2.wireOp",EDGE,"E123"),sQuery(id+"F2.wireOp",EDGE,"E124"),sQuery(id+"F2.wireOp",EDGE,"E125"),sQuery(id+"F2.wireOp",EDGE,"E126"),sQuery(id+"F2.wireOp",EDGE,"E127.1.0"),sQuery(id+"F2.wireOp",EDGE,"E127.1.1"),sQuery(id+"F2.wireOp",EDGE,"E127.1.2"),sQuery(id+"F2.wireOp",EDGE,"E127.1.3"),sQuery(id+"F2.wireOp",EDGE,"E127.1.4"),sQuery(id+"F2.wireOp",EDGE,"E127.1.5"),sQuery(id+"F2.wireOp",EDGE,"E127.1.6"),sQuery(id+"F2.wireOp",EDGE,"E127.1.7"),sQuery(id+"F2.wireOp",EDGE,"E127.1.8"),sQuery(id+"F2.wireOp",EDGE,"E127.1.9"),sQuery(id+"F2.wireOp",EDGE,"E127.1.10"),sQuery(id+"F2.wireOp",EDGE,"E127.2.0"),sQuery(id+"F2.wireOp",EDGE,"E127.2.1"),sQuery(id+"F2.wireOp",EDGE,"E127.2.2"),sQuery(id+"F2.wireOp",EDGE,"E127.2.3"),sQuery(id+"F2.wireOp",EDGE,"E127.2.4"),sQuery(id+"F2.wireOp",EDGE,"E127.2.5"),sQuery(id+"F2.wireOp",EDGE,"E127.2.6"),sQuery(id+"F2.wireOp",EDGE,"E127.2.7"),sQuery(id+"F2.wireOp",EDGE,"E127.2.8"),sQuery(id+"F2.wireOp",EDGE,"E127.2.9"),sQuery(id+"F2.wireOp",EDGE,"E127.2.10"),sQuery(id+"F2.wireOp",EDGE,"E128.trimOffspring"),sQuery(id+"F2.wireOp",EDGE,"E129.trimOffspring"),sQuery(id+"F2.wireOp",EDGE,"E130.trimOffspring"),sQuery(id+"F2.wireOp",EDGE,"E131.trimOffspring"),sQuery(id+"F2.wireOp",EDGE,"E132.trimOffspring"),sQuery(id+"F2.wireOp",EDGE,"E133.trimOffspring"),sQuery(id+"F2.wireOp",EDGE,"E134.trimOffspring"),sQuery(id+"F2.wireOp",EDGE,"E135.trimOffspring"),sQuery(id+"F2.wireOp",EDGE,"E138.bottom"),sQuery(id+"F2.wireOp",EDGE,"E138.top"),sQuery(id+"F2.wireOp",EDGE,"E138.left"),sQuery(id+"F2.wireOp",EDGE,"E138.right"),sQuery(id+"F2.wireOp",EDGE,"E139.MirrorCS"),sQuery(id+"F2.wireOp",EDGE,"E116"),sQuery(id+"F2.wireOp",EDGE,"E140.MirrorCS"),sQuery(id+"F2.wireOp",EDGE,"E141.MirrorCS"),sQuery(id+"F2.wireOp",EDGE,"E142.MirrorCS"),sQuery(id+"F2.wireOp",EDGE,"E143.MirrorCS"),sQuery(id+"F2.wireOp",EDGE,"E144.MirrorCS"),sQuery(id+"F2.wireOp",EDGE,"E145.MirrorCS"),sQuery(id+"F2.wireOp",EDGE,"E146.MirrorCS"),sQuery(id+"F2.wireOp",EDGE,"E147.MirrorCS"),sQuery(id+"F2.wireOp",EDGE,"E148.MirrorCS"),sQuery(id+"F2.wireOp",EDGE,"E149.MirrorCS"),sQuery(id+"F2.wireOp",EDGE,"E150.MirrorCS"),sQuery(id+"F2.wireOp",EDGE,"E151.MirrorCS"),sQuery(id+"F2.wireOp",EDGE,"E152.MirrorCS"),sQuery(id+"F2.wireOp",EDGE,"E153.MirrorCS"),sQuery(id+"F2.wireOp",EDGE,"E154.MirrorCS"),sQuery(id+"F2.wireOp",EDGE,"E155.MirrorCS"),sQuery(id+"F2.wireOp",EDGE,"E156.MirrorCS"),sQuery(id+"F2.wireOp",EDGE,"E157.MirrorCS"),sQuery(id+"F2.wireOp",EDGE,"E158.MirrorCS"),sQuery(id+"F2.wireOp",EDGE,"E159.MirrorCS"),sQuery(id+"F2.wireOp",EDGE,"E160.MirrorC"),sQuery(id+"F2.wireOp",EDGE,"E161.MirrorCS"),sQuery(id+"F2.wireOp",EDGE,"E162.MirrorCS"),sQuery(id+"F2.wireOp",EDGE,"E163.MirrorCS"),sQuery(id+"F2.wireOp",EDGE,"E164.MirrorCS"),sQuery(id+"F2.wireOp",EDGE,"E165.MirrorCS"),sQuery(id+"F2.wireOp",EDGE,"E166.MirrorCS"),sQuery(id+"F2.wireOp",EDGE,"E168.MirrorCS"),sQuery(id+"F2.wireOp",EDGE,"E169.MirrorCS"),sQuery(id+"F2.wireOp",EDGE,"E170.MirrorCS"),sQuery(id+"F2.wireOp",EDGE,"E171.MirrorCS"),sQuery(id+"F2.wireOp",EDGE,"E172.MirrorCS"),sQuery(id+"F2.wireOp",EDGE,"E173.MirrorCS"),sQuery(id+"F2.wireOp",EDGE,"E174.MirrorCS"),sQuery(id+"F2.wireOp",EDGE,"E175.MirrorCS"),sQuery(id+"F2.wireOp",EDGE,"E176.MirrorCS"),sQuery(id+"F2.wireOp",EDGE,"E177.MirrorCS"),sQuery(id+"F2.wireOp",EDGE,"E178.MirrorCS"),sQuery(id+"F2.wireOp",EDGE,"E179.MirrorCS"),sQuery(id+"F2.wireOp",EDGE,"E180.MirrorCS"),sQuery(id+"F2.wireOp",EDGE,"E181.MirrorCS"),sQuery(id+"F2.wireOp",EDGE,"E182.MirrorCS"),sQuery(id+"F2.wireOp",EDGE,"E183.MirrorCS"),sQuery(id+"F2.wireOp",EDGE,"E184.MirrorCS"),sQuery(id+"F2.wireOp",EDGE,"E185.MirrorCS"),sQuery(id+"F2.wireOp",EDGE,"E186.MirrorCS"),sQuery(id+"F2.wireOp",EDGE,"E187.MirrorCS"),sQuery(id+"F2.wireOp",EDGE,"E188.MirrorCS"),sQuery(id+"F2.wireOp",EDGE,"E189.MirrorCS"),sQuery(id+"F2.wireOp",EDGE,"E190.MirrorCS"),sQuery(id+"F2.wireOp",EDGE,"E191.MirrorCS"),sQuery(id+"F2.wireOp",EDGE,"E192.MirrorCS"),sQuery(id+"F2.wireOp",EDGE,"E193.MirrorCS"),sQuery(id+"F2.wireOp",EDGE,"E111"),sQuery(id+"F2.wireOp",EDGE,"E194.MirrorCS"),sQuery(id+"F2.wireOp",EDGE,"E195.MirrorCS"),sQuery(id+"F2.wireOp",EDGE,"E167.MirrorCS"),sQuery(id+"F2.wireOp",EDGE,"E196.MirrorCS"),sQuery(id+"F2.wireOp",EDGE,"E197.MirrorCS"),sQuery(id+"F2.wireOp",EDGE,"E198.MirrorCS"),sQuery(id+"F2.wireOp",EDGE,"E199.MirrorCS"),sQuery(id+"F2.wireOp",EDGE,"E200.MirrorCS"),sQuery(id+"F2.wireOp",EDGE,"E201.MirrorCS"),sQuery(id+"F2.wireOp",EDGE,"E202.MirrorCS"),sQuery(id+"F2.wireOp",EDGE,"E203.MirrorCS"),sQuery(id+"F2.wireOp",EDGE,"E204.MirrorCS"),sQuery(id+"F2.wireOp",EDGE,"E205.MirrorCS")])],"isStart":false});
            var sketch = newSketch(context, id + "F5", { "sketchPlane" : qUnion([Q0])});
            skLineSegment(sketch, "E206", {"start": v(-14.15, -60.36) * mm, "end": v(15.85, -60.36) * mm, "construction": true});
            skLineSegment(sketch, "E207", {"start": v(0.85, -60.36) * mm, "end": v(0.85, -82.72) * mm, "construction": true});
            skLineSegment(sketch, "E208", {"start": v(0.85, -60.36) * mm, "end": v(0.85, -42.59) * mm, "construction": true});
            skLineSegment(sketch, "E209.bottom", {"start": v(-26.65, -75.36) * mm, "end": v(28.35, -75.36) * mm});
            skLineSegment(sketch, "E209.top", {"start": v(-26.65, -45.36) * mm, "end": v(28.35, -45.36) * mm});
            skLineSegment(sketch, "E209.left", {"start": v(-29.15, -72.86) * mm, "end": v(-29.15, -47.86) * mm});
            skLineSegment(sketch, "E209.right", {"start": v(30.85, -72.86) * mm, "end": v(30.85, -47.86) * mm});
            skPoint(sketch, "E209.middle", {"position": v(0.85, -60.36) * mm});
            skPoint(sketch, "E210.visualSharp", {"position": v(-29.15, -45.36) * mm});
            skArc(sketch, "E210.filletArc", {"start": v(-26.65, -45.36) * mm, "mid": v(-28.41, -46.1) * mm, "end": v(-29.15, -47.86) * mm});
            skPoint(sketch, "E211.visualSharp", {"position": v(-29.15, -75.36) * mm});
            skArc(sketch, "E211.filletArc", {"start": v(-29.15, -72.86) * mm, "mid": v(-28.41, -74.63) * mm, "end": v(-26.65, -75.36) * mm});
            skPoint(sketch, "E212.visualSharp", {"position": v(30.85, -75.36) * mm});
            skArc(sketch, "E212.filletArc", {"start": v(28.35, -75.36) * mm, "mid": v(30.12, -74.63) * mm, "end": v(30.85, -72.86) * mm});
            skPoint(sketch, "E213.visualSharp", {"position": v(30.85, -45.36) * mm});
            skArc(sketch, "E213.filletArc", {"start": v(30.85, -47.86) * mm, "mid": v(30.12, -46.1) * mm, "end": v(28.35, -45.36) * mm});
            skSolve(sketch);
        }
        {
            var Q0;
            Q0 = qSketchRegion(id + "F5", true);
            extrude(context, id + "F6", {"entities" : qUnion([Q0]), "depth" : 4 * mm, "offsetDistance" : 25 * mm});
        }
        {
            var Q0;
            Q0=makeQuery(id+"F6.opExtrude","CAP_FACE",FACE,{"disambiguationData":[OSD([sQuery(id+"F5.wireOp",EDGE,"E209.bottom"),sQuery(id+"F5.wireOp",EDGE,"E209.top"),sQuery(id+"F5.wireOp",EDGE,"E209.left"),sQuery(id+"F5.wireOp",EDGE,"E209.right"),sQuery(id+"F5.wireOp",EDGE,"E210.filletArc"),sQuery(id+"F5.wireOp",EDGE,"E211.filletArc"),sQuery(id+"F5.wireOp",EDGE,"E212.filletArc"),sQuery(id+"F5.wireOp",EDGE,"E213.filletArc")])],"isStart":false});
            var sketch = newSketch(context, id + "F7", { "sketchPlane" : qUnion([Q0])});
            skPoint(sketch, "E214.0", {"position": v(-14.15, -60.36) * mm});
            skPoint(sketch, "E214.1", {"position": v(15.85, -60.36) * mm});
            skSolve(sketch);
        }
        {
            var Q0;
            Q0=sQuery(id+"F7.wireOp",VERTEX,"E214.1");
            var Q1;
            Q1=sQuery(id+"F7.wireOp",VERTEX,"E214.0");
            var Q2;
            Q2=makeQuery(id+"F6.opExtrude","SWEPT_BODY",BODY,{"disambiguationData":[OSD([sQuery(id+"F5.wireOp",EDGE,"E209.bottom"),sQuery(id+"F5.wireOp",EDGE,"E209.top"),sQuery(id+"F5.wireOp",EDGE,"E209.left"),sQuery(id+"F5.wireOp",EDGE,"E209.right"),sQuery(id+"F5.wireOp",EDGE,"E210.filletArc"),sQuery(id+"F5.wireOp",EDGE,"E211.filletArc"),sQuery(id+"F5.wireOp",EDGE,"E212.filletArc"),sQuery(id+"F5.wireOp",EDGE,"E213.filletArc")])]});
            hole(context, id + "F8", {"style" : HoleStyle.C_SINK, "endStyle" : HoleEndStyle.THROUGH, "holeDiameter" : 6.8 * mm, "cSinkDiameter" : 10 * mm, "cSinkAngle" : 90 * degree, "majorDiameter" : 5 * mm, "isTappedThrough" : true, "tappedDepth" : 12 * mm, "tapClearance" : 3, "locations" : qUnion([Q0, Q1]), "scope" : qUnion([Q2])});
        }
        {
            var Q0;
            Q0=makeQuery(id+"F6.opExtrude","CAP_FACE",FACE,{"disambiguationData":[OSD([sQuery(id+"F5.wireOp",EDGE,"E209.bottom"),sQuery(id+"F5.wireOp",EDGE,"E209.top"),sQuery(id+"F5.wireOp",EDGE,"E209.left"),sQuery(id+"F5.wireOp",EDGE,"E209.right"),sQuery(id+"F5.wireOp",EDGE,"E210.filletArc"),sQuery(id+"F5.wireOp",EDGE,"E211.filletArc"),sQuery(id+"F5.wireOp",EDGE,"E212.filletArc"),sQuery(id+"F5.wireOp",EDGE,"E213.filletArc")])],"isStart":true});
            var sketch = newSketch(context, id + "F9", { "sketchPlane" : qUnion([Q0])});
            skLineSegment(sketch, "E215.0", {"start": v(-20.1, 56.18) * mm, "end": v(-22.4, 53.88) * mm});
            skLineSegment(sketch, "E215.1", {"start": v(-20.1, 64.55) * mm, "end": v(-20.1, 56.18) * mm});
            skLineSegment(sketch, "E215.2", {"start": v(-22.4, 66.85) * mm, "end": v(-20.1, 64.55) * mm});
            skPoint(sketch, "E216.0", {"position": v(-22.4, 50.56) * mm});
            skPoint(sketch, "E217.0", {"position": v(-22.4, 70.17) * mm});
            skLineSegment(sketch, "E218", {"start": v(-22.4, 53.88) * mm, "end": v(-22.4, 66.85) * mm});
            skLineSegment(sketch, "E219.0", {"start": v(21.8, 56.18) * mm, "end": v(23.08, 54.9) * mm});
            skLineSegment(sketch, "E219.1", {"start": v(21.8, 64.55) * mm, "end": v(21.8, 56.18) * mm});
            skLineSegment(sketch, "E219.2", {"start": v(23.08, 65.82) * mm, "end": v(21.8, 64.55) * mm});
            skPoint(sketch, "E220.0", {"position": v(24.1, 50.56) * mm});
            skPoint(sketch, "E220.1", {"position": v(24.1, 70.17) * mm});
            skLineSegment(sketch, "E221", {"start": v(24.1, 55.33) * mm, "end": v(24.1, 65.4) * mm});
            skPoint(sketch, "E222.visualSharp", {"position": v(24.1, 66.85) * mm});
            skArc(sketch, "E222.filletArc", {"start": v(24.1, 65.4) * mm, "mid": v(23.73, 65.95) * mm, "end": v(23.08, 65.82) * mm});
            skPoint(sketch, "E223.visualSharp", {"position": v(24.1, 53.88) * mm});
            skArc(sketch, "E223.filletArc", {"start": v(23.08, 54.9) * mm, "mid": v(23.73, 54.78) * mm, "end": v(24.1, 55.33) * mm});
            skSolve(sketch);
        }
        {
            var Q0;
            Q0 = qSketchRegion(id + "F9", true);
            extrude(context, id + "F10", {"entities" : qUnion([Q0]), "operationType" : NewBodyOperationType.ADD, "depth" : 8 * mm, "offsetDistance" : 25 * mm});
        }
        {
            var Q0;
            Q0=makeQuery(id+"F6.opExtrude","SWEPT_FACE",FACE,{"disambiguationData":[OSD([sQuery(id+"F5.wireOp",EDGE,"E209.right")])]});
            var sketch = newSketch(context, id + "F11", { "sketchPlane" : qUnion([Q0])});
            skLineSegment(sketch, "E224.0", {"start": v(-72.86, 304) * mm, "end": v(-47.86, 304) * mm});
            skLineSegment(sketch, "E224.1", {"start": v(-72.86, 300) * mm, "end": v(-47.86, 300) * mm});
            skLineSegment(sketch, "E225.0", {"start": v(-75.36, 304) * mm, "end": v(-75.36, 300) * mm});
            skLineSegment(sketch, "E225.1", {"start": v(-72.86, 304) * mm, "end": v(-75.36, 304) * mm});
            skLineSegment(sketch, "E225.2", {"start": v(-72.86, 300) * mm, "end": v(-75.36, 300) * mm});
            skLineSegment(sketch, "E225.3", {"start": v(-45.36, 300) * mm, "end": v(-47.86, 300) * mm});
            skLineSegment(sketch, "E225.4", {"start": v(-45.36, 304) * mm, "end": v(-45.36, 300) * mm});
            skLineSegment(sketch, "E225.5", {"start": v(-45.36, 304) * mm, "end": v(-47.86, 304) * mm});
            skLineSegment(sketch, "E226.0", {"start": v(-66.85, 297) * mm, "end": v(-66.85, 300) * mm});
            skLineSegment(sketch, "E226.1", {"start": v(-53.88, 297) * mm, "end": v(-53.88, 300) * mm});
            skLineSegment(sketch, "E227", {"start": v(-61.85, 292) * mm, "end": v(-58.88, 292) * mm});
            skPoint(sketch, "E228.visualSharp", {"position": v(-66.85, 292) * mm});
            skArc(sketch, "E228.filletArc", {"start": v(-66.85, 297) * mm, "mid": v(-65.38, 293.46) * mm, "end": v(-61.85, 292) * mm});
            skPoint(sketch, "E229.visualSharp", {"position": v(-53.88, 292) * mm});
            skArc(sketch, "E229.filletArc", {"start": v(-58.88, 292) * mm, "mid": v(-55.35, 293.46) * mm, "end": v(-53.88, 297) * mm});
            skCircle(sketch, "E230", {"center": v(-60.36, 296) * mm, "radius": 1.5 * mm});
            skSolve(sketch);
        }
        {
            var Q0;
            Q0 = qSketchRegion(id + "F11", true);
            extrude(context, id + "F12", {"entities" : qUnion([Q0]), "operationType" : NewBodyOperationType.INTERSECT, "endBound" : BoundingType.UP_TO_NEXT, "oppositeDirection" : true, "depth" : 25 * mm, "offsetDistance" : 25 * mm});
        }
    });
